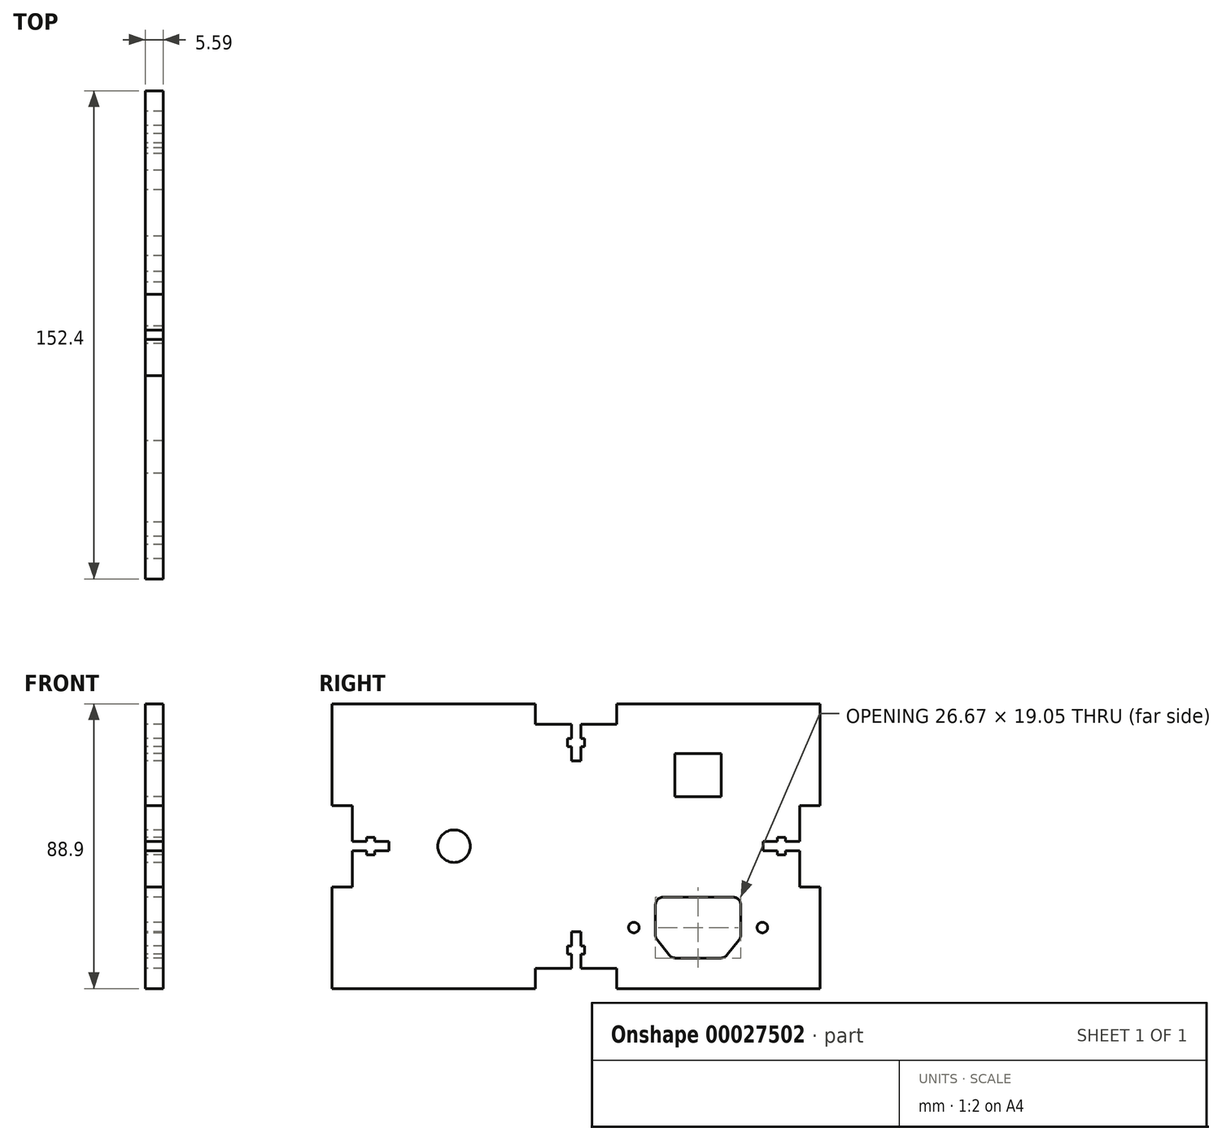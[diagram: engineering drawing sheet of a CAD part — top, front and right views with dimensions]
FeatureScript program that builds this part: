
annotation { "Feature Type Name" : "Feature", "Feature Type Description" : "" }
export const myFeature = defineFeature(function(context is Context, id is Id, definition is map)
    precondition{}
    {
        {
            var Q0;
            Q0=qCreatedBy(makeId("Right.planeOp"),FACE);
            var sketch = newSketch(context, id + "F0", { "sketchPlane" : qUnion([Q0])});
            skLineSegment(sketch, "E0.rect.bottom", {"start": v(76.2, 44.45) * mm, "end": v(12.7, 44.45) * mm});
            skLineSegment(sketch, "E0.rect.top", {"start": v(76.2, -44.45) * mm, "end": v(12.7, -44.45) * mm});
            skLineSegment(sketch, "E0.rect.left", {"start": v(76.2, 44.45) * mm, "end": v(76.2, 12.7) * mm});
            skLineSegment(sketch, "E0.rect.right", {"start": v(-76.2, 44.45) * mm, "end": v(-76.2, 12.7) * mm});
            skPoint(sketch, "E0.rect.middle", {"position": v(0, 0) * mm});
            skLineSegment(sketch, "E1", {"start": v(-76.2, 0) * mm, "end": v(0, 0) * mm, "construction": true});
            skLineSegment(sketch, "E2", {"start": v(0, 0) * mm, "end": v(76.2, 0) * mm, "construction": true});
            skLineSegment(sketch, "E3", {"start": v(38.1, 0) * mm, "end": v(38.1, -15.88) * mm, "construction": true});
            skLineSegment(sketch, "E4.rect.bottom", {"start": v(48.9, -15.88) * mm, "end": v(38.1, -15.88) * mm});
            skLineSegment(sketch, "E4.rect.left", {"start": v(51.44, -18.42) * mm, "end": v(51.44, -27.68) * mm});
            skLineSegment(sketch, "E4.rect.right", {"start": v(24.77, -18.42) * mm, "end": v(24.77, -27.68) * mm});
            skPoint(sketch, "E4.rect.middle", {"position": v(38.1, -22.22) * mm});
            skLineSegment(sketch, "E5.0", {"start": v(29.84, 0) * mm, "end": v(29.84, -44.45) * mm, "construction": true});
            skLineSegment(sketch, "E6.0", {"start": v(46.35, 0) * mm, "end": v(46.35, -44.45) * mm, "construction": true});
            skLineSegment(sketch, "E7.0", {"start": v(50.1, -34.92) * mm, "end": v(24.7, -34.92) * mm, "construction": true});
            skLineSegment(sketch, "E8", {"start": v(25.32, -29.27) * mm, "end": v(29.08, -33.97) * mm});
            skLineSegment(sketch, "E9", {"start": v(31.07, -34.92) * mm, "end": v(38.1, -34.92) * mm});
            skLineSegment(sketch, "E10", {"start": v(47.12, -33.97) * mm, "end": v(50.88, -29.27) * mm});
            skLineSegment(sketch, "E11", {"start": v(38.1, 0) * mm, "end": v(38.1, 44.45) * mm, "construction": true});
            skLineSegment(sketch, "E12.rect.bottom", {"start": v(45.34, 15.5) * mm, "end": v(30.86, 15.5) * mm});
            skLineSegment(sketch, "E12.rect.top", {"start": v(45.34, 28.96) * mm, "end": v(30.86, 28.96) * mm});
            skLineSegment(sketch, "E12.rect.left", {"start": v(45.34, 15.5) * mm, "end": v(45.34, 28.96) * mm});
            skLineSegment(sketch, "E12.rect.right", {"start": v(30.86, 15.5) * mm, "end": v(30.86, 28.96) * mm});
            skPoint(sketch, "E12.rect.middle", {"position": v(38.1, 22.23) * mm});
            skCircle(sketch, "E13", {"center": v(-38.1, 0) * mm, "radius": 5.08 * mm});
            skPoint(sketch, "E14.visualSharp", {"position": v(24.77, -15.88) * mm});
            skArc(sketch, "E14.filletArc", {"start": v(27.3, -15.88) * mm, "mid": v(25.5, -16.62) * mm, "end": v(24.77, -18.42) * mm});
            skPoint(sketch, "E15.visualSharp", {"position": v(51.44, -15.88) * mm});
            skArc(sketch, "E15.filletArc", {"start": v(51.44, -18.42) * mm, "mid": v(50.7, -16.62) * mm, "end": v(48.9, -15.88) * mm});
            skPoint(sketch, "E16.visualSharp", {"position": v(51.44, -28.58) * mm});
            skArc(sketch, "E16.filletArc", {"start": v(50.88, -29.27) * mm, "mid": v(51.3, -28.52) * mm, "end": v(51.44, -27.68) * mm});
            skPoint(sketch, "E17.visualSharp", {"position": v(24.77, -28.58) * mm});
            skArc(sketch, "E17.filletArc", {"start": v(24.76, -27.68) * mm, "mid": v(24.9, -28.52) * mm, "end": v(25.32, -29.27) * mm});
            skPoint(sketch, "E18.visualSharp", {"position": v(29.85, -34.92) * mm});
            skArc(sketch, "E18.filletArc", {"start": v(29.08, -33.97) * mm, "mid": v(29.97, -34.67) * mm, "end": v(31.07, -34.92) * mm});
            skPoint(sketch, "E19.visualSharp", {"position": v(46.36, -34.92) * mm});
            skArc(sketch, "E19.filletArc", {"start": v(45.13, -34.92) * mm, "mid": v(46.23, -34.67) * mm, "end": v(47.12, -33.97) * mm});
            skLineSegment(sketch, "E20", {"start": v(38.1, -15.88) * mm, "end": v(27.3, -15.88) * mm});
            skLineSegment(sketch, "E21", {"start": v(38.1, -15.88) * mm, "end": v(38.1, -34.92) * mm, "construction": true});
            skLineSegment(sketch, "E22", {"start": v(38.1, -34.92) * mm, "end": v(45.13, -34.92) * mm});
            skLineSegment(sketch, "E23", {"start": v(38.1, -34.92) * mm, "end": v(38.1, -44.45) * mm, "construction": true});
            skLineSegment(sketch, "E24", {"start": v(19.69, -25.4) * mm, "end": v(56.52, -25.4) * mm, "construction": true});
            skPoint(sketch, "E24.startSnap0", {"position": v(38.1, -25.4) * mm});
            skCircle(sketch, "E25", {"center": v(18.05, -25.4) * mm, "radius": 1.65 * mm});
            skCircle(sketch, "E26", {"center": v(58.18, -25.4) * mm, "radius": 1.65 * mm});
            skLineSegment(sketch, "E27.0", {"start": v(-69.85, 38.1) * mm, "end": v(-69.85, -38.1) * mm, "construction": true});
            skLineSegment(sketch, "E27.1", {"start": v(69.85, 38.1) * mm, "end": v(1.46, 38.1) * mm, "construction": true});
            skLineSegment(sketch, "E27.2", {"start": v(69.85, 38.1) * mm, "end": v(69.85, -38.1) * mm, "construction": true});
            skLineSegment(sketch, "E27.3", {"start": v(69.85, -38.1) * mm, "end": v(-69.85, -38.1) * mm, "construction": true});
            skLineSegment(sketch, "E28", {"start": v(0, 44.45) * mm, "end": v(0, 38.1) * mm, "construction": true});
            skLineSegment(sketch, "E29.0", {"start": v(-12.7, 44.45) * mm, "end": v(-12.7, 38.1) * mm, "construction": true});
            skLineSegment(sketch, "E30.0", {"start": v(12.7, 44.45) * mm, "end": v(12.7, -44.45) * mm, "construction": true});
            skLineSegment(sketch, "E31.0", {"start": v(-76.2, -12.7) * mm, "end": v(0, -12.7) * mm, "construction": true});
            skLineSegment(sketch, "E32.0", {"start": v(-76.2, 12.7) * mm, "end": v(-69.85, 12.7) * mm, "construction": true});
            skLineSegment(sketch, "E33", {"start": v(-12.7, 26.67) * mm, "end": v(12.7, 26.67) * mm, "construction": true});
            skLineSegment(sketch, "E34", {"start": v(-12.7, 38.1) * mm, "end": v(-12.7, 26.67) * mm, "construction": true});
            skLineSegment(sketch, "E35", {"start": v(-12.7, 26.67) * mm, "end": v(-12.7, -44.45) * mm, "construction": true});
            skLineSegment(sketch, "E36", {"start": v(-12.7, 32.38) * mm, "end": v(12.7, 32.38) * mm, "construction": true});
            skLineSegment(sketch, "E37.0", {"start": v(-1.46, 44.45) * mm, "end": v(-1.46, -44.45) * mm, "construction": true});
            skLineSegment(sketch, "E38.0", {"start": v(1.46, 44.45) * mm, "end": v(1.46, -44.45) * mm, "construction": true});
            skLineSegment(sketch, "E39.0", {"start": v(-2.7, 44.45) * mm, "end": v(-2.7, -44.45) * mm, "construction": true});
            skLineSegment(sketch, "E40.MirrorCS", {"start": v(2.7, 44.45) * mm, "end": v(2.7, -44.45) * mm, "construction": true});
            skLineSegment(sketch, "E41.0", {"start": v(-12.7, 31.11) * mm, "end": v(12.7, 31.11) * mm, "construction": true});
            skLineSegment(sketch, "E42.MirrorCS", {"start": v(-12.7, 33.65) * mm, "end": v(12.7, 33.65) * mm, "construction": true});
            skLineSegment(sketch, "E43", {"start": v(-1.46, 44.45) * mm, "end": v(-1.46, 33.65) * mm, "construction": true});
            skLineSegment(sketch, "E44", {"start": v(-1.46, 33.65) * mm, "end": v(-2.7, 33.65) * mm, "construction": true});
            skLineSegment(sketch, "E45", {"start": v(-2.7, 33.65) * mm, "end": v(-2.7, 31.11) * mm, "construction": true});
            skLineSegment(sketch, "E46", {"start": v(-2.7, 31.11) * mm, "end": v(-1.46, 31.11) * mm, "construction": true});
            skLineSegment(sketch, "E47", {"start": v(-1.46, 31.11) * mm, "end": v(-1.46, 26.67) * mm, "construction": true});
            skLineSegment(sketch, "E48", {"start": v(-1.46, 26.67) * mm, "end": v(1.46, 26.67) * mm, "construction": true});
            skLineSegment(sketch, "E49", {"start": v(1.46, 26.67) * mm, "end": v(1.46, 31.11) * mm, "construction": true});
            skLineSegment(sketch, "E50", {"start": v(1.46, 31.11) * mm, "end": v(2.7, 31.11) * mm, "construction": true});
            skLineSegment(sketch, "E51", {"start": v(2.7, 31.11) * mm, "end": v(2.7, 33.65) * mm, "construction": true});
            skLineSegment(sketch, "E52", {"start": v(2.7, 33.65) * mm, "end": v(1.46, 33.65) * mm, "construction": true});
            skLineSegment(sketch, "E53", {"start": v(1.46, 33.65) * mm, "end": v(1.46, 44.45) * mm, "construction": true});
            skLineSegment(sketch, "E54", {"start": v(-1.46, 38.1) * mm, "end": v(-1.46, 33.65) * mm});
            skLineSegment(sketch, "E55", {"start": v(-2.7, 33.65) * mm, "end": v(-2.7, 31.11) * mm});
            skLineSegment(sketch, "E56", {"start": v(-1.46, 31.11) * mm, "end": v(-1.46, 26.67) * mm});
            skLineSegment(sketch, "E57", {"start": v(1.46, 26.67) * mm, "end": v(1.46, 31.11) * mm});
            skLineSegment(sketch, "E58", {"start": v(2.7, 31.11) * mm, "end": v(2.7, 33.65) * mm});
            skLineSegment(sketch, "E59", {"start": v(1.46, 33.65) * mm, "end": v(1.46, 38.1) * mm});
            skLineSegment(sketch, "E60", {"start": v(-1.46, 26.67) * mm, "end": v(1.46, 26.67) * mm});
            skLineSegment(sketch, "E61", {"start": v(1.46, 33.65) * mm, "end": v(2.7, 33.65) * mm});
            skLineSegment(sketch, "E62", {"start": v(1.46, 31.11) * mm, "end": v(2.7, 31.11) * mm});
            skLineSegment(sketch, "E63", {"start": v(-1.46, 31.11) * mm, "end": v(-2.7, 31.11) * mm});
            skLineSegment(sketch, "E64", {"start": v(-2.7, 33.65) * mm, "end": v(-1.46, 33.65) * mm});
            skLineSegment(sketch, "E65.MirrorCS", {"start": v(1.46, -33.65) * mm, "end": v(1.46, -38.1) * mm});
            skLineSegment(sketch, "E66.MirrorCS", {"start": v(-1.46, -38.1) * mm, "end": v(-1.46, -33.65) * mm});
            skLineSegment(sketch, "E67.MirrorCS", {"start": v(-2.7, -33.65) * mm, "end": v(-1.46, -33.65) * mm});
            skLineSegment(sketch, "E68.MirrorCS", {"start": v(-2.7, -33.65) * mm, "end": v(-2.7, -31.11) * mm});
            skLineSegment(sketch, "E69.MirrorCS", {"start": v(-1.46, -31.11) * mm, "end": v(-2.7, -31.11) * mm});
            skLineSegment(sketch, "E70.MirrorCS", {"start": v(-1.46, -31.11) * mm, "end": v(-1.46, -26.67) * mm});
            skLineSegment(sketch, "E71.MirrorCS", {"start": v(-1.46, -26.67) * mm, "end": v(1.46, -26.67) * mm});
            skLineSegment(sketch, "E72.MirrorCS", {"start": v(1.46, -26.67) * mm, "end": v(1.46, -31.11) * mm});
            skLineSegment(sketch, "E73.MirrorCS", {"start": v(1.46, -31.11) * mm, "end": v(2.7, -31.11) * mm});
            skLineSegment(sketch, "E74.MirrorCS", {"start": v(2.7, -31.11) * mm, "end": v(2.7, -33.65) * mm});
            skLineSegment(sketch, "E75.MirrorCS", {"start": v(1.46, -33.65) * mm, "end": v(2.7, -33.65) * mm});
            skLineSegment(sketch, "E76", {"start": v(-12.7, -44.45) * mm, "end": v(-12.7, -38.1) * mm});
            skLineSegment(sketch, "E77", {"start": v(-12.7, -38.1) * mm, "end": v(-1.46, -38.1) * mm});
            skLineSegment(sketch, "E78", {"start": v(12.7, -38.1) * mm, "end": v(12.7, -44.45) * mm});
            skLineSegment(sketch, "E79.trimOffspring", {"start": v(-12.7, -44.45) * mm, "end": v(-76.2, -44.45) * mm});
            skPoint(sketch, "E80.orphan", {"position": v(-1.46, -44.45) * mm});
            skPoint(sketch, "E81.orphan", {"position": v(1.46, -44.45) * mm});
            skLineSegment(sketch, "E82.trimOffspring", {"start": v(1.46, -38.1) * mm, "end": v(12.7, -38.1) * mm});
            skLineSegment(sketch, "E83", {"start": v(-12.7, 44.45) * mm, "end": v(-12.7, 38.1) * mm});
            skLineSegment(sketch, "E84", {"start": v(-12.7, 38.1) * mm, "end": v(-1.46, 38.1) * mm});
            skLineSegment(sketch, "E85", {"start": v(12.7, 38.1) * mm, "end": v(12.7, 44.45) * mm});
            skLineSegment(sketch, "E86.trimOffspring", {"start": v(-12.7, 44.45) * mm, "end": v(-76.2, 44.45) * mm});
            skLineSegment(sketch, "E87.trimOffspring", {"start": v(1.46, 38.1) * mm, "end": v(12.7, 38.1) * mm});
            skLineSegment(sketch, "E88.trimOffspring", {"start": v(0, 32.38) * mm, "end": v(0, 31.11) * mm, "construction": true});
            skLineSegment(sketch, "E89.trimOffspring", {"start": v(-1.46, 38.1) * mm, "end": v(-69.85, 38.1) * mm, "construction": true});
            skLineSegment(sketch, "E90.trimOffspring", {"start": v(0, 26.67) * mm, "end": v(0, -44.45) * mm, "construction": true});
            skLineSegment(sketch, "E91.0", {"start": v(-76.2, -1.46) * mm, "end": v(0, -1.46) * mm, "construction": true});
            skLineSegment(sketch, "E92.MirrorCS", {"start": v(-76.2, 1.46) * mm, "end": v(0, 1.46) * mm, "construction": true});
            skLineSegment(sketch, "E93.0", {"start": v(-76.2, -2.7) * mm, "end": v(0, -2.7) * mm, "construction": true});
            skLineSegment(sketch, "E94.MirrorCS", {"start": v(-76.2, 2.7) * mm, "end": v(0, 2.7) * mm, "construction": true});
            skLineSegment(sketch, "E95", {"start": v(-58.42, 12.7) * mm, "end": v(-58.42, -12.7) * mm, "construction": true});
            skLineSegment(sketch, "E96", {"start": v(-69.85, 12.7) * mm, "end": v(-58.42, 12.7) * mm, "construction": true});
            skLineSegment(sketch, "E97", {"start": v(-58.42, 12.7) * mm, "end": v(0, 12.7) * mm, "construction": true});
            skLineSegment(sketch, "E98", {"start": v(-64.13, 12.7) * mm, "end": v(-64.13, -12.7) * mm, "construction": true});
            skLineSegment(sketch, "E99.0", {"start": v(-65.4, 12.7) * mm, "end": v(-65.4, 1.46) * mm});
            skLineSegment(sketch, "E100.MirrorCS", {"start": v(-62.86, 12.7) * mm, "end": v(-62.86, -12.7) * mm, "construction": true});
            skLineSegment(sketch, "E101", {"start": v(-69.85, 1.46) * mm, "end": v(-65.4, 1.46) * mm});
            skLineSegment(sketch, "E102", {"start": v(-65.4, 1.46) * mm, "end": v(-65.4, 2.7) * mm});
            skLineSegment(sketch, "E103", {"start": v(-65.4, 2.7) * mm, "end": v(-62.86, 2.7) * mm});
            skLineSegment(sketch, "E104", {"start": v(-62.86, 2.7) * mm, "end": v(-62.86, 1.46) * mm});
            skLineSegment(sketch, "E105", {"start": v(-62.86, 1.46) * mm, "end": v(-58.42, 1.46) * mm});
            skLineSegment(sketch, "E106", {"start": v(-58.42, 1.46) * mm, "end": v(-58.42, -1.46) * mm});
            skLineSegment(sketch, "E107", {"start": v(-58.42, -1.46) * mm, "end": v(-62.86, -1.46) * mm});
            skLineSegment(sketch, "E108", {"start": v(-62.86, -1.46) * mm, "end": v(-62.86, -2.7) * mm});
            skLineSegment(sketch, "E109", {"start": v(-62.86, -2.7) * mm, "end": v(-65.4, -2.7) * mm});
            skLineSegment(sketch, "E110", {"start": v(-65.4, -2.7) * mm, "end": v(-65.4, -1.46) * mm});
            skLineSegment(sketch, "E111", {"start": v(-65.4, -1.46) * mm, "end": v(-69.85, -1.46) * mm});
            skLineSegment(sketch, "E112", {"start": v(-69.85, -1.46) * mm, "end": v(-69.85, -12.7) * mm});
            skLineSegment(sketch, "E113", {"start": v(-69.85, -12.7) * mm, "end": v(-76.2, -12.7) * mm});
            skLineSegment(sketch, "E114", {"start": v(-69.85, 1.46) * mm, "end": v(-69.85, 12.7) * mm});
            skLineSegment(sketch, "E115", {"start": v(-69.85, 12.7) * mm, "end": v(-76.2, 12.7) * mm});
            skLineSegment(sketch, "E116.trimOffspring", {"start": v(-76.2, -12.7) * mm, "end": v(-76.2, -44.45) * mm});
            skLineSegment(sketch, "E117.trimOffspring", {"start": v(-65.4, -1.46) * mm, "end": v(-65.4, -12.7) * mm});
            skLineSegment(sketch, "E118.MirrorCS", {"start": v(69.85, 12.7) * mm, "end": v(76.2, 12.7) * mm});
            skLineSegment(sketch, "E119.MirrorCS", {"start": v(69.85, 1.46) * mm, "end": v(69.85, 12.7) * mm});
            skLineSegment(sketch, "E120.MirrorCS", {"start": v(69.85, -1.46) * mm, "end": v(69.85, -12.7) * mm});
            skLineSegment(sketch, "E121.MirrorCS", {"start": v(69.85, -12.7) * mm, "end": v(76.2, -12.7) * mm});
            skLineSegment(sketch, "E122.MirrorCS", {"start": v(65.4, -1.46) * mm, "end": v(69.85, -1.46) * mm});
            skLineSegment(sketch, "E123.MirrorCS", {"start": v(65.4, -2.7) * mm, "end": v(65.4, -1.46) * mm});
            skLineSegment(sketch, "E124.MirrorCS", {"start": v(62.86, -2.7) * mm, "end": v(65.4, -2.7) * mm});
            skLineSegment(sketch, "E125.MirrorCS", {"start": v(62.86, -1.46) * mm, "end": v(62.86, -2.7) * mm});
            skLineSegment(sketch, "E126.MirrorCS", {"start": v(58.42, -1.46) * mm, "end": v(62.86, -1.46) * mm});
            skLineSegment(sketch, "E127.MirrorCS", {"start": v(58.42, 1.46) * mm, "end": v(58.42, -1.46) * mm});
            skLineSegment(sketch, "E128.MirrorCS", {"start": v(62.86, 1.46) * mm, "end": v(58.42, 1.46) * mm});
            skLineSegment(sketch, "E129.MirrorCS", {"start": v(62.86, 2.7) * mm, "end": v(62.86, 1.46) * mm});
            skLineSegment(sketch, "E130.MirrorCS", {"start": v(65.4, 2.7) * mm, "end": v(62.86, 2.7) * mm});
            skLineSegment(sketch, "E131.MirrorCS", {"start": v(65.4, 1.46) * mm, "end": v(65.4, 2.7) * mm});
            skLineSegment(sketch, "E132.MirrorCS", {"start": v(69.85, 1.46) * mm, "end": v(65.4, 1.46) * mm});
            skLineSegment(sketch, "E133.trimOffspring", {"start": v(76.2, -12.7) * mm, "end": v(76.2, -44.45) * mm});
            skSolve(sketch);
        }
        {
            var Q0;
            Q0=makeQuery(id+"F0.imprint","IMPRINT",FACE,{"disambiguationData":[TD([[makeQuery(id+"F0.imprint","IMPRINT",EDGE,{"derivedFrom":sQuery(id+"F0.wireOp",EDGE,"E0.rect.bottom")}),1.0]])]});
            extrude(context, id + "F1", {"entities" : qUnion([Q0]), "depth" : 5.6 * mm});
        }
    });
